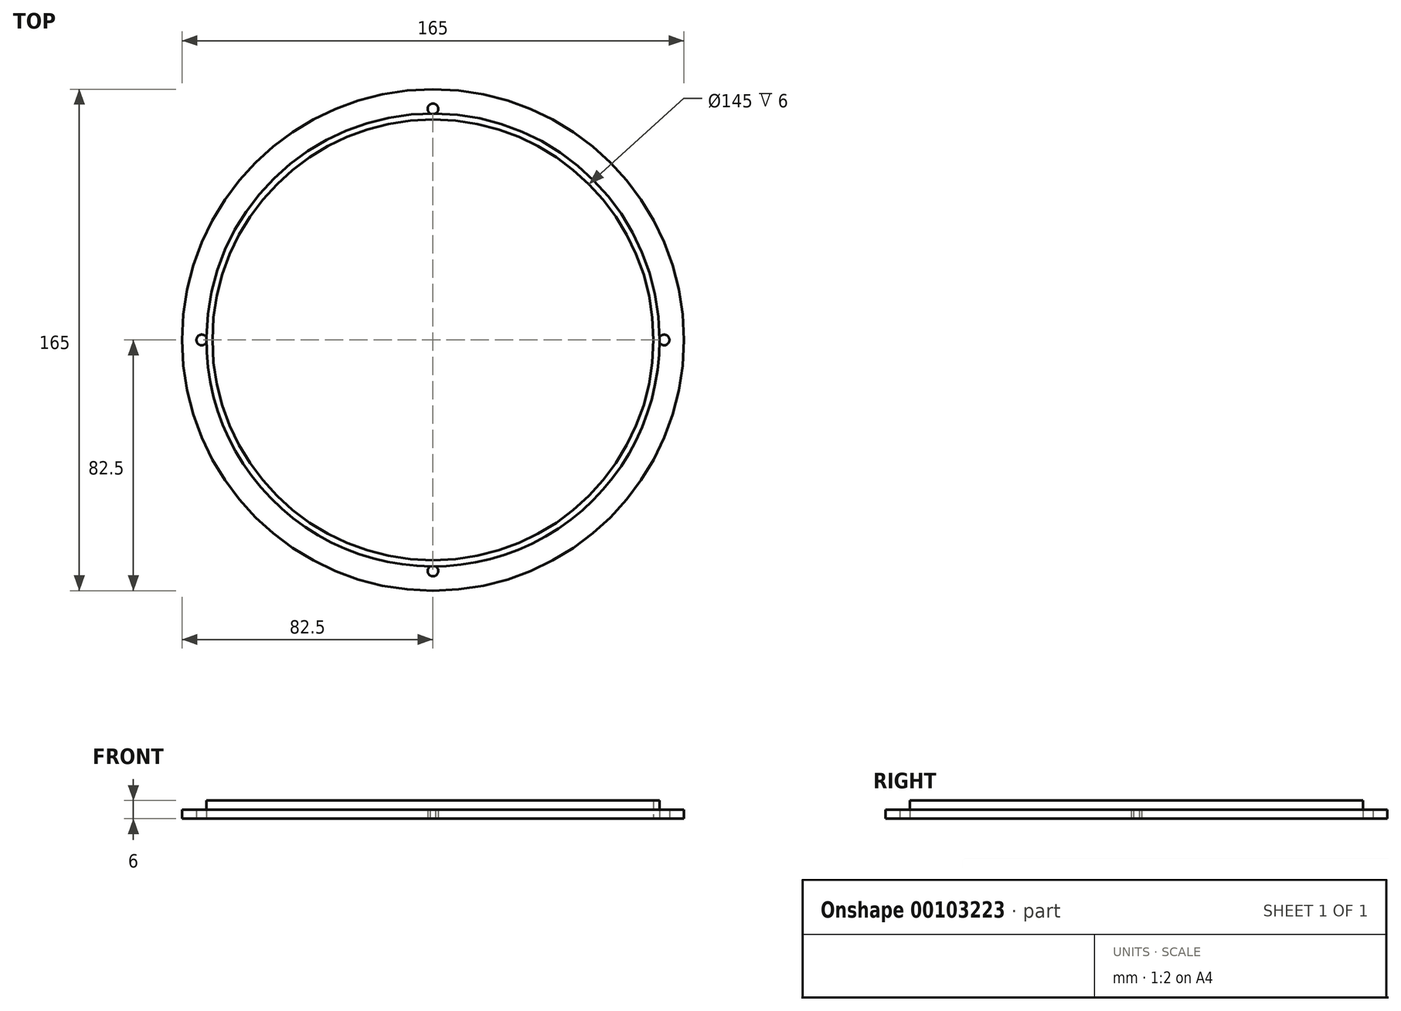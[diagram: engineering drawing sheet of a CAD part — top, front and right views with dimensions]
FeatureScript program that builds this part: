
annotation { "Feature Type Name" : "Feature", "Feature Type Description" : "" }
export const myFeature = defineFeature(function(context is Context, id is Id, definition is map)
    precondition{}
    {
        {
            var Q0;
            Q0=qCreatedBy(makeId("Top.planeOp"),FACE);
            var sketch = newSketch(context, id + "F0", { "sketchPlane" : qUnion([Q0])});
            skCircle(sketch, "E0", {"center": v(0, 0) * mm, "radius": 82.5 * mm});
            skCircle(sketch, "E1", {"center": v(0, 0) * mm, "radius": 72.5 * mm});
            skPoint(sketch, "E2", {"position": v(0, 76) * mm});
            skPoint(sketch, "E3.1.0", {"position": v(-76, 0) * mm});
            skPoint(sketch, "E3.2.0", {"position": v(0, -76) * mm});
            skPoint(sketch, "E3.3.0", {"position": v(76, 0) * mm});
            skCircle(sketch, "E4", {"center": v(0, 0) * mm, "radius": 74.5 * mm});
            skSolve(sketch);
        }
        {
            var Q0;
            Q0=makeQuery(id+"F0.imprint","IMPRINT",FACE,{"disambiguationData":[TD([[makeQuery(id+"F0.imprint","IMPRINT",EDGE,{"derivedFrom":sQuery(id+"F0.wireOp",EDGE,"E0")}),1.0]])]});
            extrude(context, id + "F1", {"entities" : qUnion([Q0]), "depth" : 3 * mm});
        }
        {
            var Q0;
            Q0=sQuery(id+"F0.wireOp",VERTEX,"E2");
            var Q1;
            Q1=sQuery(id+"F0.wireOp",VERTEX,"E3.1.0");
            var Q2;
            Q2=sQuery(id+"F0.wireOp",VERTEX,"E3.2.0");
            var Q3;
            Q3=sQuery(id+"F0.wireOp",VERTEX,"E3.3.0");
            var Q4;
            Q4=makeQuery(id+"F1.opExtrude","SWEPT_BODY",BODY,{"disambiguationData":[OSD([sQuery(id+"F0.wireOp",EDGE,"E0"),sQuery(id+"F0.wireOp",EDGE,"E1")])]});
            hole(context, id + "F2", {"style" : HoleStyle.SIMPLE, "endStyle" : HoleEndStyle.BLIND, "oppositeDirection" : true, "holeDiameter" : 3.5 * mm, "holeDepth" : 5 * mm, "locations" : qUnion([Q0, Q1, Q2, Q3]), "scope" : qUnion([Q4])});
        }
        {
            var Q0;
            Q0=makeQuery(id+"F0.imprint","IMPRINT",FACE,{"disambiguationData":[TD([[makeQuery(id+"F0.imprint","IMPRINT",EDGE,{"derivedFrom":sQuery(id+"F0.wireOp",EDGE,"E1")}),-1.0]])]});
            extrude(context, id + "F3", {"entities" : qUnion([Q0]), "operationType" : NewBodyOperationType.ADD, "depth" : 6 * mm});
        }
    });
